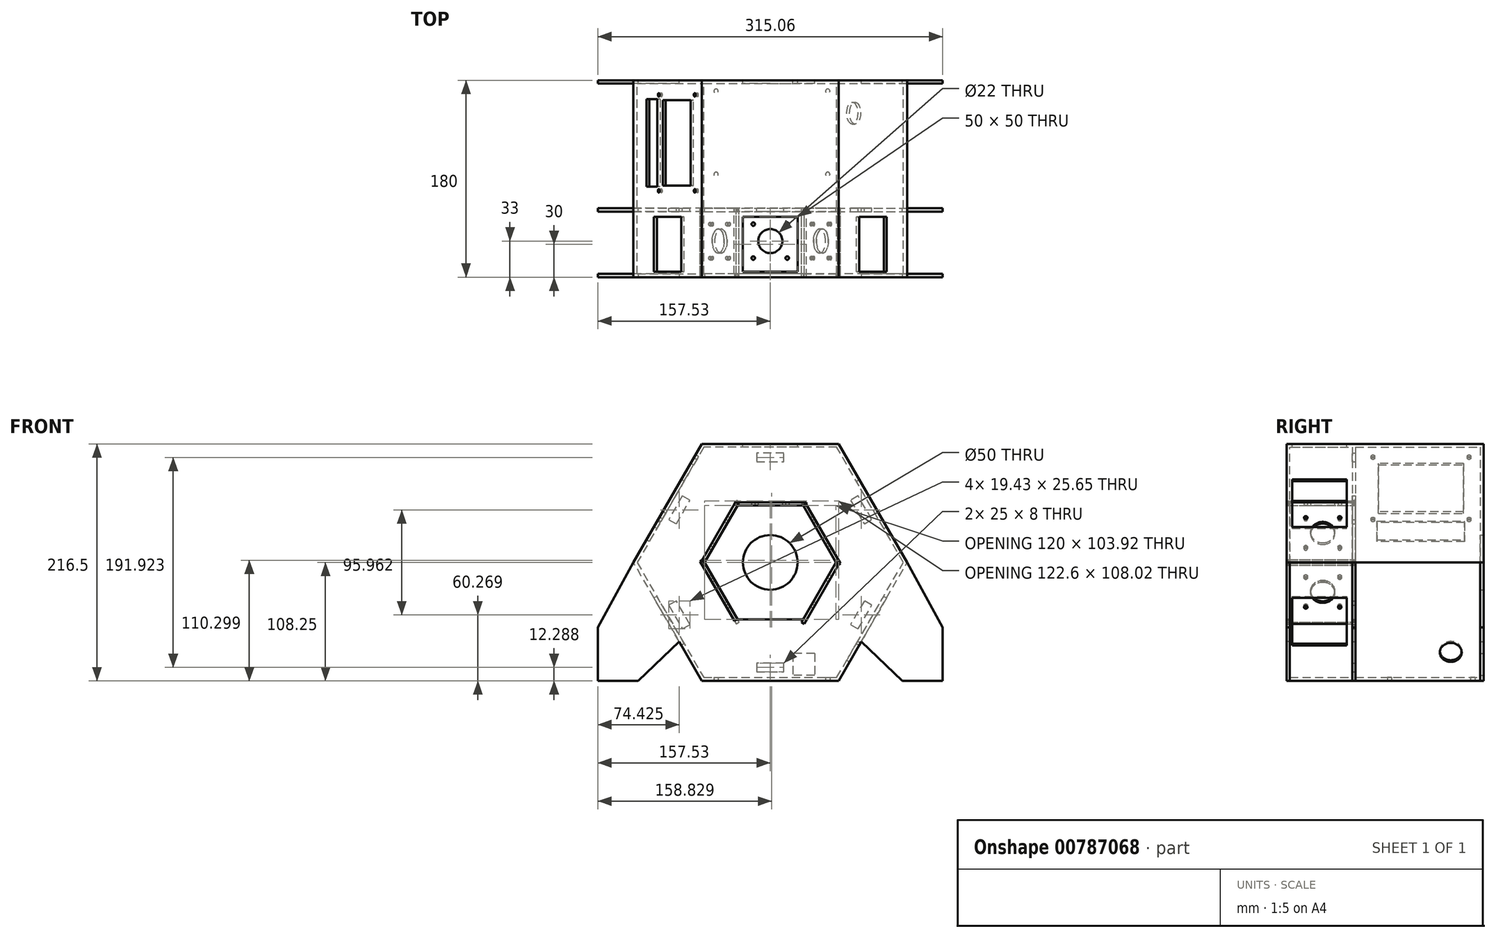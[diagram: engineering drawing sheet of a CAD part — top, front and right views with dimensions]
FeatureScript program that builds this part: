
annotation { "Feature Type Name" : "Feature", "Feature Type Description" : "" }
export const myFeature = defineFeature(function(context is Context, id is Id, definition is map)
    precondition{}
    {
        {
            var Q0;
            Q0=qCreatedBy(makeId("Front.planeOp"),FACE);
            var sketch = newSketch(context, id + "F0", { "sketchPlane" : qUnion([Q0])});
            skCircle(sketch, "E0.cCircle", {"center": v(0, 0) * mm, "radius": 108.25 * mm, "construction": true});
            skLineSegment(sketch, "E0.0", {"start": v(62.5, 108.25) * mm, "end": v(125, 0) * mm});
            skLineSegment(sketch, "E0.1", {"start": v(125, 0) * mm, "end": v(62.5, -108.25) * mm});
            skLineSegment(sketch, "E0.2", {"start": v(62.5, -108.25) * mm, "end": v(-62.5, -108.25) * mm});
            skLineSegment(sketch, "E0.3", {"start": v(-62.5, -108.25) * mm, "end": v(-125, 0) * mm});
            skLineSegment(sketch, "E0.4", {"start": v(-125, 0) * mm, "end": v(-62.5, 108.25) * mm});
            skLineSegment(sketch, "E0.5", {"start": v(-62.5, 108.25) * mm, "end": v(62.5, 108.25) * mm});
            skPoint(sketch, "E0.0.midPoint", {"position": v(93.75, 54.13) * mm});
            skSolve(sketch);
        }
        {
            var Q0;
            Q0=makeQuery(id+"F0.imprint","IMPRINT",FACE,{"disambiguationData":[TD([[makeQuery(id+"F0.imprint","IMPRINT",EDGE,{"derivedFrom":sQuery(id+"F0.wireOp",EDGE,"E0.0")}),-1.0]])]});
            extrude(context, id + "F1", {"entities" : qUnion([Q0]), "depth" : 180 * mm, "offsetDistance" : 25 * mm});
        }
        {
            var Q0;
            Q0=makeQuery(id+"F1.opExtrude","CAP_FACE",FACE,{"disambiguationData":[OSD([sQuery(id+"F0.wireOp",EDGE,"E0.0"),sQuery(id+"F0.wireOp",EDGE,"E0.1"),sQuery(id+"F0.wireOp",EDGE,"E0.2"),sQuery(id+"F0.wireOp",EDGE,"E0.3"),sQuery(id+"F0.wireOp",EDGE,"E0.4"),sQuery(id+"F0.wireOp",EDGE,"E0.5")])],"isStart":false});
            shell(context, id + "F2", {"entities" : qUnion([Q0]), "thickness" : 3 * mm});
        }
        {
            var Q0;
            Q0=makeQuery(id+"F1.opExtrude","CAP_FACE",FACE,{"disambiguationData":[OSD([sQuery(id+"F0.wireOp",EDGE,"E0.0"),sQuery(id+"F0.wireOp",EDGE,"E0.1"),sQuery(id+"F0.wireOp",EDGE,"E0.2"),sQuery(id+"F0.wireOp",EDGE,"E0.3"),sQuery(id+"F0.wireOp",EDGE,"E0.4"),sQuery(id+"F0.wireOp",EDGE,"E0.5")])],"isStart":false});
            var sketch = newSketch(context, id + "F3", { "sketchPlane" : qUnion([Q0])});
            skLineSegment(sketch, "E1.0", {"start": v(-60.77, 105.25) * mm, "end": v(60.77, 105.25) * mm});
            skLineSegment(sketch, "E2.0", {"start": v(60.77, 105.25) * mm, "end": v(121.54, 0) * mm});
            skLineSegment(sketch, "E3.0", {"start": v(121.54, 0) * mm, "end": v(60.77, -105.25) * mm});
            skLineSegment(sketch, "E3.1", {"start": v(60.77, -105.25) * mm, "end": v(-60.77, -105.25) * mm});
            skLineSegment(sketch, "E3.2", {"start": v(-60.77, -105.25) * mm, "end": v(-121.54, 0) * mm});
            skLineSegment(sketch, "E3.3", {"start": v(-121.54, 0) * mm, "end": v(-60.77, 105.25) * mm});
            skCircle(sketch, "E4.cCircle", {"center": v(0, 0) * mm, "radius": 51.96 * mm, "construction": true});
            skLineSegment(sketch, "E4.0", {"start": v(60, 0) * mm, "end": v(30, -51.96) * mm});
            skLineSegment(sketch, "E4.1", {"start": v(30, -51.96) * mm, "end": v(-30, -51.96) * mm});
            skLineSegment(sketch, "E4.2", {"start": v(-30, -51.96) * mm, "end": v(-60, 0) * mm});
            skLineSegment(sketch, "E4.3", {"start": v(-60, 0) * mm, "end": v(-30, 51.96) * mm});
            skLineSegment(sketch, "E4.4", {"start": v(-30, 51.96) * mm, "end": v(30, 51.96) * mm});
            skLineSegment(sketch, "E4.5", {"start": v(30, 51.96) * mm, "end": v(60, 0) * mm});
            skPoint(sketch, "E4.0.midPoint", {"position": v(45, -25.98) * mm});
            skSolve(sketch);
        }
        {
            var Q0;
            Q0=makeQuery(id+"F3.imprint","IMPRINT",FACE,{"disambiguationData":[TD([[makeQuery(id+"F3.imprint","IMPRINT",EDGE,{"derivedFrom":sQuery(id+"F3.wireOp",EDGE,"E1.0")}),-1.0]])]});
            extrude(context, id + "F4", {"entities" : qUnion([Q0]), "operationType" : NewBodyOperationType.ADD, "oppositeDirection" : true, "depth" : 3 * mm, "offsetDistance" : 25 * mm});
        }
        {
            var Q0;
            Q0=makeQuery(id+"F1.opExtrude","CAP_FACE",FACE,{"disambiguationData":[OSD([sQuery(id+"F0.wireOp",EDGE,"E0.0"),sQuery(id+"F0.wireOp",EDGE,"E0.1"),sQuery(id+"F0.wireOp",EDGE,"E0.2"),sQuery(id+"F0.wireOp",EDGE,"E0.3"),sQuery(id+"F0.wireOp",EDGE,"E0.4"),sQuery(id+"F0.wireOp",EDGE,"E0.5")])],"isStart":true});
            var sketch = newSketch(context, id + "F5", { "sketchPlane" : qUnion([Q0])});
            skPoint(sketch, "E5", {"position": v(0, 0) * mm});
            skSolve(sketch);
        }
        {
            var Q0;
            Q0=sQuery(id+"F5.wireOp",VERTEX,"E5");
            var Q1;
            Q1=makeQuery(id+"F1.opExtrude","SWEPT_BODY",BODY,{"disambiguationData":[OSD([sQuery(id+"F0.wireOp",EDGE,"E0.0"),sQuery(id+"F0.wireOp",EDGE,"E0.1"),sQuery(id+"F0.wireOp",EDGE,"E0.2"),sQuery(id+"F0.wireOp",EDGE,"E0.3"),sQuery(id+"F0.wireOp",EDGE,"E0.4"),sQuery(id+"F0.wireOp",EDGE,"E0.5")])]});
            hole(context, id + "F6", {"style" : HoleStyle.SIMPLE, "endStyle" : HoleEndStyle.THROUGH, "holeDiameter" : 50 * mm, "majorDiameter" : 5 * mm, "isTappedThrough" : true, "tappedDepth" : 12 * mm, "tapClearance" : 3, "locations" : qUnion([Q0]), "scope" : qUnion([Q1])});
        }
        {
            var Q0;
            Q0=makeQuery(id+"F4.opExtrude","SWEPT_FACE",FACE,{"disambiguationData":[OSD([sQuery(id+"F3.wireOp",EDGE,"E4.5")])]});
            var sketch = newSketch(context, id + "F7", { "sketchPlane" : qUnion([Q0])});
            skLineSegment(sketch, "E6.bottom", {"start": v(177, 30) * mm, "end": v(117, 30) * mm});
            skLineSegment(sketch, "E6.top", {"start": v(180, -30) * mm, "end": v(117, -30) * mm});
            skLineSegment(sketch, "E6.left", {"start": v(180, 30) * mm, "end": v(180, -30) * mm});
            skLineSegment(sketch, "E6.right", {"start": v(117, 30) * mm, "end": v(117, -30) * mm});
            skCircle(sketch, "E7", {"center": v(147, 0) * mm, "radius": 11 * mm});
            skCircle(sketch, "E8", {"center": v(162.5, 15.5) * mm, "radius": 1.6 * mm});
            skCircle(sketch, "E9", {"center": v(162.5, -15.5) * mm, "radius": 1.6 * mm});
            skCircle(sketch, "E10", {"center": v(131.5, -15.5) * mm, "radius": 1.6 * mm});
            skCircle(sketch, "E11", {"center": v(131.5, 15.5) * mm, "radius": 1.6 * mm});
            skLineSegment(sketch, "E12.top", {"start": v(177, 33) * mm, "end": v(117, 33) * mm});
            skLineSegment(sketch, "E12.left", {"start": v(177, 30) * mm, "end": v(177, 33) * mm});
            skLineSegment(sketch, "E12.right", {"start": v(117, 30) * mm, "end": v(117, 33) * mm});
            skLineSegment(sketch, "E13.bottom", {"start": v(180, -30) * mm, "end": v(120, -30) * mm});
            skLineSegment(sketch, "E13.top", {"start": v(180, -33) * mm, "end": v(120, -33) * mm});
            skLineSegment(sketch, "E13.left", {"start": v(180, -30) * mm, "end": v(180, -33) * mm});
            skLineSegment(sketch, "E13.right", {"start": v(120, -30) * mm, "end": v(120, -33) * mm});
            skSolve(sketch);
        }
        {
            var Q0;
            Q0=makeQuery(id+"F7.imprint","IMPRINT",FACE,{"disambiguationData":[TD([[makeQuery(id+"F7.imprint","IMPRINT",EDGE,{"derivedFrom":sQuery(id+"F7.wireOp",EDGE,"E6.bottom")}),-1.0]])]});
            var Q1;
            {var subQ0=sQuery(id+"F7.wireOp",EDGE,"E6.top");Q1=makeQuery(id+"F7.imprint","IMPRINT",FACE,{"disambiguationData":[TD([[makeQuery(id+"F7.imprint","IMPRINT",EDGE,{"derivedFrom":subQ0}),-1.0]])]});}
            var Q2;
            {var subQ0=sQuery(id+"F7.wireOp",EDGE,"E6.left");Q2=makeQuery(id+"F7.imprint","IMPRINT",FACE,{"disambiguationData":[TD([[makeQuery(id+"F7.imprint","IMPRINT",EDGE,{"derivedFrom":subQ0}),-1.0]])]});}
            var Q3;
            Q3=makeQuery(id+"F7.imprint","IMPRINT",FACE,{"disambiguationData":[TD([[makeQuery(id+"F7.imprint","IMPRINT",EDGE,{"derivedFrom":sQuery(id+"F7.wireOp",EDGE,"E13.top")}),-1.0]])]});
            extrude(context, id + "F8", {"entities" : qUnion([Q0, Q1, Q2, Q3]), "oppositeDirection" : true, "depth" : 3 * mm, "offsetDistance" : 25 * mm});
        }
        {
            var Q0;
            Q0=qCreatedBy(makeId("Right.planeOp"),FACE);
            var sketch = newSketch(context, id + "F9", { "sketchPlane" : qUnion([Q0])});
            skLineSegment(sketch, "E14", {"start": v(0, 0) * mm, "end": v(-423.8, 0) * mm, "construction": true});
            skSolve(sketch);
        }
        {
            var Q0;
            Q0=makeQuery(id+"F8.opExtrude","SWEPT_BODY",BODY,{"disambiguationData":[OSD([sQuery(id+"F7.wireOp",EDGE,"E6.bottom"),sQuery(id+"F7.wireOp",EDGE,"E6.top"),sQuery(id+"F7.wireOp",EDGE,"E6.left"),sQuery(id+"F7.wireOp",EDGE,"E6.right"),sQuery(id+"F7.wireOp",EDGE,"E7"),sQuery(id+"F7.wireOp",EDGE,"E8"),sQuery(id+"F7.wireOp",EDGE,"E9"),sQuery(id+"F7.wireOp",EDGE,"E10"),sQuery(id+"F7.wireOp",EDGE,"E11")])]});
            var Q1;
            Q1=sQuery(id+"F9.wireOp",EDGE,"E14");
            circularPattern(context, id + "F10", {"entities" : qUnion([Q0]), "axis" : qUnion([Q1]), "angle" : 360 * degree, "instanceCount" : 6, "equalSpace" : true});
        }
        {
            var Q0;
            Q0=makeQuery(id+"F10.opPattern","COPY",BODY,{"derivedFrom":makeQuery(id+"F8.opExtrude","SWEPT_BODY",BODY,{"disambiguationData":[OSD([sQuery(id+"F7.wireOp",EDGE,"E6.bottom"),sQuery(id+"F7.wireOp",EDGE,"E6.top"),sQuery(id+"F7.wireOp",EDGE,"E6.left"),sQuery(id+"F7.wireOp",EDGE,"E6.right"),sQuery(id+"F7.wireOp",EDGE,"E7"),sQuery(id+"F7.wireOp",EDGE,"E8"),sQuery(id+"F7.wireOp",EDGE,"E9"),sQuery(id+"F7.wireOp",EDGE,"E10"),sQuery(id+"F7.wireOp",EDGE,"E11")])]}),"instanceName":"4"});
            deleteBodies(context, id + "F11", {"entities" : qUnion([Q0])});
        }
        {
            var Q0;
            Q0=makeQuery(id+"F8.opExtrude","SWEPT_FACE",FACE,{"disambiguationData":[OSD([sQuery(id+"F7.wireOp",EDGE,"E6.right"),sQuery(id+"F7.wireOp",EDGE,"E12.right")])]});
            var sketch = newSketch(context, id + "F12", { "sketchPlane" : qUnion([Q0])});
            skLineSegment(sketch, "E15.0", {"start": v(-60, 0) * mm, "end": v(-28.5, 54.56) * mm});
            skLineSegment(sketch, "E16.0", {"start": v(-62.5, 108.25) * mm, "end": v(-125, 0) * mm});
            skLineSegment(sketch, "E17.0", {"start": v(62.5, 108.25) * mm, "end": v(-62.5, 108.25) * mm});
            skLineSegment(sketch, "E18.0", {"start": v(125, 0) * mm, "end": v(62.5, 108.25) * mm});
            skLineSegment(sketch, "E18.1", {"start": v(62.5, -108.25) * mm, "end": v(125, 0) * mm});
            skLineSegment(sketch, "E18.2", {"start": v(-62.5, -108.25) * mm, "end": v(62.5, -108.25) * mm});
            skLineSegment(sketch, "E18.3", {"start": v(-125, 0) * mm, "end": v(-62.5, -108.25) * mm});
            skLineSegment(sketch, "E19.0", {"start": v(-30, 51.96) * mm, "end": v(33, 51.96) * mm});
            skLineSegment(sketch, "E19.1", {"start": v(30, 51.96) * mm, "end": v(61.5, -2.6) * mm});
            skLineSegment(sketch, "E20.0", {"start": v(60, 0) * mm, "end": v(28.5, -54.56) * mm});
            skLineSegment(sketch, "E20.1", {"start": v(-30, -51.96) * mm, "end": v(30, -51.96) * mm});
            skLineSegment(sketch, "E20.2", {"start": v(-30, -51.96) * mm, "end": v(-61.5, 2.6) * mm});
            skSolve(sketch);
        }
        {
            var Q0;
            Q0=makeQuery(id+"F12.imprint","IMPRINT",FACE,{"disambiguationData":[TD([[makeQuery(id+"F12.imprint","IMPRINT",EDGE,{"derivedFrom":sQuery(id+"F12.wireOp",EDGE,"E16.0")}),1.0]])]});
            extrude(context, id + "F13", {"entities" : qUnion([Q0]), "oppositeDirection" : true, "depth" : 3 * mm, "offsetDistance" : 25 * mm});
        }
        {
            var Q0;
            Q0=makeQuery(id+"F1.opExtrude","SWEPT_FACE",FACE,{"disambiguationData":[OSD([sQuery(id+"F0.wireOp",EDGE,"E0.4")])]});
            var sketch = newSketch(context, id + "F14", { "sketchPlane" : qUnion([Q0])});
            skLineSegment(sketch, "E21.bottom", {"start": v(18.19, 42.08) * mm, "end": v(96.19, 42.08) * mm});
            skLineSegment(sketch, "E21.top", {"start": v(18.19, -8.92) * mm, "end": v(96.19, -8.92) * mm});
            skLineSegment(sketch, "E21.left", {"start": v(18.19, 42.08) * mm, "end": v(18.19, -8.92) * mm});
            skLineSegment(sketch, "E21.right", {"start": v(96.19, 42.08) * mm, "end": v(96.19, -8.92) * mm});
            skCircle(sketch, "E22", {"center": v(13.29, -16.32) * mm, "radius": 1.6 * mm});
            skCircle(sketch, "E23", {"center": v(13.29, 49.48) * mm, "radius": 1.6 * mm});
            skCircle(sketch, "E24", {"center": v(101.09, 49.48) * mm, "radius": 1.6 * mm});
            skCircle(sketch, "E25", {"center": v(101.09, -16.32) * mm, "radius": 1.6 * mm});
            skLineSegment(sketch, "E26.bottom", {"start": v(97.37, -38.8) * mm, "end": v(17.37, -38.8) * mm});
            skLineSegment(sketch, "E26.top", {"start": v(97.37, -18.8) * mm, "end": v(17.37, -18.8) * mm});
            skLineSegment(sketch, "E26.left", {"start": v(97.37, -38.8) * mm, "end": v(97.37, -18.8) * mm});
            skLineSegment(sketch, "E26.right", {"start": v(17.37, -38.8) * mm, "end": v(17.37, -18.8) * mm});
            skPoint(sketch, "E26.middle", {"position": v(57.37, -28.8) * mm});
            skSolve(sketch);
        }
        {
            var Q0;
            Q0 = qSketchRegion(id + "F14", true);
            extrude(context, id + "F15", {"entities" : qUnion([Q0]), "operationType" : NewBodyOperationType.REMOVE, "endBound" : BoundingType.UP_TO_NEXT, "oppositeDirection" : true, "depth" : 25 * mm, "offsetDistance" : 25 * mm});
        }
        {
            var Q0;
            Q0=makeQuery(id+"F1.opExtrude","SWEPT_FACE",FACE,{"disambiguationData":[OSD([sQuery(id+"F0.wireOp",EDGE,"E0.1")])]});
            var sketch = newSketch(context, id + "F16", { "sketchPlane" : qUnion([Q0])});
            skPoint(sketch, "E27", {"position": v(-30, -32.5) * mm});
            skSolve(sketch);
        }
        {
            var Q0;
            Q0=sQuery(id+"F16.wireOp",VERTEX,"E27");
            var Q1;
            Q1=makeQuery(id+"F1.opExtrude","SWEPT_BODY",BODY,{"disambiguationData":[OSD([sQuery(id+"F0.wireOp",EDGE,"E0.0"),sQuery(id+"F0.wireOp",EDGE,"E0.1"),sQuery(id+"F0.wireOp",EDGE,"E0.2"),sQuery(id+"F0.wireOp",EDGE,"E0.3"),sQuery(id+"F0.wireOp",EDGE,"E0.4"),sQuery(id+"F0.wireOp",EDGE,"E0.5")])]});
            hole(context, id + "F17", {"style" : HoleStyle.SIMPLE, "endStyle" : HoleEndStyle.BLIND, "holeDiameter" : 20 * mm, "majorDiameter" : 5 * mm, "holeDepth" : 3 * mm, "isTappedThrough" : true, "tappedDepth" : 12 * mm, "tapClearance" : 3, "locations" : qUnion([Q0]), "scope" : qUnion([Q1])});
        }
        {
            var Q0;
            Q0=makeQuery(id+"F1.opExtrude","CAP_FACE",FACE,{"disambiguationData":[OSD([sQuery(id+"F0.wireOp",EDGE,"E0.0"),sQuery(id+"F0.wireOp",EDGE,"E0.1"),sQuery(id+"F0.wireOp",EDGE,"E0.2"),sQuery(id+"F0.wireOp",EDGE,"E0.3"),sQuery(id+"F0.wireOp",EDGE,"E0.4"),sQuery(id+"F0.wireOp",EDGE,"E0.5")])],"isStart":true});
            var sketch = newSketch(context, id + "F18", { "sketchPlane" : qUnion([Q0])});
            skLineSegment(sketch, "E28.bottom", {"start": v(-40.5, -83.25) * mm, "end": v(-20.5, -83.25) * mm});
            skLineSegment(sketch, "E28.top", {"start": v(-40.5, -103.25) * mm, "end": v(-20.5, -103.25) * mm});
            skLineSegment(sketch, "E28.left", {"start": v(-40.5, -83.25) * mm, "end": v(-40.5, -103.25) * mm});
            skLineSegment(sketch, "E28.right", {"start": v(-20.5, -83.25) * mm, "end": v(-20.5, -103.25) * mm});
            skSolve(sketch);
        }
        {
            var Q0;
            Q0=makeQuery(id+"F18.imprint","IMPRINT",FACE,{"disambiguationData":[TD([[makeQuery(id+"F18.imprint","IMPRINT",EDGE,{"derivedFrom":sQuery(id+"F18.wireOp",EDGE,"E28.bottom")}),-1.0]])]});
            extrude(context, id + "F19", {"entities" : qUnion([Q0]), "operationType" : NewBodyOperationType.REMOVE, "endBound" : BoundingType.UP_TO_NEXT, "oppositeDirection" : true, "depth" : 25 * mm, "offsetDistance" : 25 * mm});
        }
        {
            var Q0;
            Q0=makeQuery(id+"F13.opExtrude","CAP_FACE",FACE,{"disambiguationData":[OSD([sQuery(id+"F7.wireOp",EDGE,"E6.top"),sQuery(id+"F7.wireOp",EDGE,"E6.right"),sQuery(id+"F7.wireOp",EDGE,"E12.top"),sQuery(id+"F7.wireOp",EDGE,"E12.right"),sQuery(id+"F12.wireOp",EDGE,"E15.0"),sQuery(id+"F12.wireOp",EDGE,"E16.0"),sQuery(id+"F12.wireOp",EDGE,"E17.0"),sQuery(id+"F12.wireOp",EDGE,"E18.0"),sQuery(id+"F12.wireOp",EDGE,"E18.1"),sQuery(id+"F12.wireOp",EDGE,"E18.2"),sQuery(id+"F12.wireOp",EDGE,"E18.3"),sQuery(id+"F12.wireOp",EDGE,"E19.0"),sQuery(id+"F12.wireOp",EDGE,"E19.1"),sQuery(id+"F12.wireOp",EDGE,"E20.0"),sQuery(id+"F12.wireOp",EDGE,"E20.1"),sQuery(id+"F12.wireOp",EDGE,"E20.2")])],"isStart":true});
            var sketch = newSketch(context, id + "F20", { "sketchPlane" : qUnion([Q0])});
            skLineSegment(sketch, "E29.bottom", {"start": v(12.5, 99.96) * mm, "end": v(-12.5, 99.96) * mm});
            skLineSegment(sketch, "E29.top", {"start": v(12.5, 91.96) * mm, "end": v(-12.5, 91.96) * mm});
            skLineSegment(sketch, "E29.left", {"start": v(12.5, 99.96) * mm, "end": v(12.5, 91.96) * mm});
            skLineSegment(sketch, "E29.right", {"start": v(-12.5, 99.96) * mm, "end": v(-12.5, 91.96) * mm});
            skPoint(sketch, "E29.middle", {"position": v(0, 95.96) * mm});
            skLineSegment(sketch, "E30.1.0", {"start": v(-80.32, 60.8) * mm, "end": v(-73.4, 56.8) * mm});
            skLineSegment(sketch, "E30.1.1", {"start": v(-80.32, 60.8) * mm, "end": v(-92.82, 39.16) * mm});
            skLineSegment(sketch, "E30.1.2", {"start": v(-92.82, 39.16) * mm, "end": v(-85.9, 35.16) * mm});
            skLineSegment(sketch, "E30.1.3", {"start": v(-73.4, 56.8) * mm, "end": v(-85.9, 35.16) * mm});
            skLineSegment(sketch, "E30.2.0", {"start": v(-92.82, -39.16) * mm, "end": v(-85.9, -35.16) * mm});
            skLineSegment(sketch, "E30.2.1", {"start": v(-92.82, -39.16) * mm, "end": v(-80.32, -60.8) * mm});
            skLineSegment(sketch, "E30.2.2", {"start": v(-80.32, -60.8) * mm, "end": v(-73.4, -56.8) * mm});
            skLineSegment(sketch, "E30.2.3", {"start": v(-85.9, -35.16) * mm, "end": v(-73.4, -56.8) * mm});
            skLineSegment(sketch, "E30.3.0", {"start": v(-12.5, -99.96) * mm, "end": v(-12.5, -91.96) * mm});
            skLineSegment(sketch, "E30.3.1", {"start": v(-12.5, -99.96) * mm, "end": v(12.5, -99.96) * mm});
            skLineSegment(sketch, "E30.3.2", {"start": v(12.5, -99.96) * mm, "end": v(12.5, -91.96) * mm});
            skLineSegment(sketch, "E30.3.3", {"start": v(-12.5, -91.96) * mm, "end": v(12.5, -91.96) * mm});
            skLineSegment(sketch, "E30.4.0", {"start": v(80.32, -60.8) * mm, "end": v(73.4, -56.8) * mm});
            skLineSegment(sketch, "E30.4.1", {"start": v(80.32, -60.8) * mm, "end": v(92.82, -39.16) * mm});
            skLineSegment(sketch, "E30.4.2", {"start": v(92.82, -39.16) * mm, "end": v(85.9, -35.16) * mm});
            skLineSegment(sketch, "E30.4.3", {"start": v(73.4, -56.8) * mm, "end": v(85.9, -35.16) * mm});
            skLineSegment(sketch, "E30.5.0", {"start": v(92.82, 39.16) * mm, "end": v(85.9, 35.16) * mm});
            skLineSegment(sketch, "E30.5.1", {"start": v(92.82, 39.16) * mm, "end": v(80.32, 60.8) * mm});
            skLineSegment(sketch, "E30.5.2", {"start": v(80.32, 60.8) * mm, "end": v(73.4, 56.8) * mm});
            skLineSegment(sketch, "E30.5.3", {"start": v(85.9, 35.16) * mm, "end": v(73.4, 56.8) * mm});
            skPoint(sketch, "E30.center", {"position": v(0, 0) * mm});
            skSolve(sketch);
        }
        {
            var Q0;
            Q0 = qSketchRegion(id + "F20", true);
            extrude(context, id + "F21", {"entities" : qUnion([Q0]), "operationType" : NewBodyOperationType.REMOVE, "endBound" : BoundingType.UP_TO_NEXT, "oppositeDirection" : true, "depth" : 25 * mm, "offsetDistance" : 25 * mm});
        }
        {
            var Q0;
            Q0=makeQuery(id+"F1.opExtrude","SWEPT_FACE",FACE,{"disambiguationData":[OSD([sQuery(id+"F0.wireOp",EDGE,"E0.2")])]});
            var sketch = newSketch(context, id + "F22", { "sketchPlane" : qUnion([Q0])});
            skLineSegment(sketch, "E31.bottom", {"start": v(-49.5, 10) * mm, "end": v(52.5, 10) * mm});
            skLineSegment(sketch, "E31.top", {"start": v(-49.5, 86) * mm, "end": v(52.5, 86) * mm});
            skLineSegment(sketch, "E31.left", {"start": v(-49.5, 10) * mm, "end": v(-49.5, 86) * mm});
            skLineSegment(sketch, "E31.right", {"start": v(52.5, 10) * mm, "end": v(52.5, 86) * mm});
            skCircle(sketch, "E32", {"center": v(-49.5, 10) * mm, "radius": 2 * mm});
            skCircle(sketch, "E33", {"center": v(-49.5, 86) * mm, "radius": 2 * mm});
            skCircle(sketch, "E34", {"center": v(52.5, 86) * mm, "radius": 2 * mm});
            skCircle(sketch, "E35", {"center": v(52.5, 10) * mm, "radius": 2 * mm});
            skSolve(sketch);
        }
        {
            var Q0;
            {var subQ0=sQuery(id+"F22.wireOp",EDGE,"E31.right");var subQ1=sQuery(id+"F22.wireOp",EDGE,"E31.bottom");var subQ2=makeQuery(id+"F22.imprint","INTERSECT",VERTEX,{"derivedFrom":[subQ1,subQ0]});Q0=makeQuery(id+"F22.imprint","IMPRINT",FACE,{"disambiguationData":[TD([[makeQuery(id+"F22.imprint","IMPRINT",EDGE,{"disambiguationData":[TD([[subQ2,1.0]])],"derivedFrom":subQ1}),-1.0]])]});}
            var Q1;
            {var subQ0=sQuery(id+"F22.wireOp",EDGE,"E31.right");var subQ1=sQuery(id+"F22.wireOp",EDGE,"E31.bottom");var subQ2=makeQuery(id+"F22.imprint","INTERSECT",VERTEX,{"derivedFrom":[subQ1,subQ0]});Q1=makeQuery(id+"F22.imprint","IMPRINT",FACE,{"disambiguationData":[TD([[makeQuery(id+"F22.imprint","IMPRINT",EDGE,{"disambiguationData":[TD([[subQ2,1.0]])],"derivedFrom":subQ1}),1.0]])]});}
            var Q2;
            {var subQ0=sQuery(id+"F22.wireOp",EDGE,"E31.left");var subQ1=sQuery(id+"F22.wireOp",EDGE,"E31.bottom");var subQ2=makeQuery(id+"F22.imprint","INTERSECT",VERTEX,{"derivedFrom":[subQ1,subQ0]});Q2=makeQuery(id+"F22.imprint","IMPRINT",FACE,{"disambiguationData":[TD([[makeQuery(id+"F22.imprint","IMPRINT",EDGE,{"disambiguationData":[TD([[subQ2,-1.0]])],"derivedFrom":subQ1}),1.0]])]});}
            var Q3;
            {var subQ0=sQuery(id+"F22.wireOp",EDGE,"E31.left");var subQ1=sQuery(id+"F22.wireOp",EDGE,"E31.bottom");var subQ2=makeQuery(id+"F22.imprint","INTERSECT",VERTEX,{"derivedFrom":[subQ1,subQ0]});Q3=makeQuery(id+"F22.imprint","IMPRINT",FACE,{"disambiguationData":[TD([[makeQuery(id+"F22.imprint","IMPRINT",EDGE,{"disambiguationData":[TD([[subQ2,-1.0]])],"derivedFrom":subQ1}),-1.0]])]});}
            var Q4;
            {var subQ0=sQuery(id+"F22.wireOp",EDGE,"E31.left");var subQ1=sQuery(id+"F22.wireOp",EDGE,"E31.top");var subQ2=makeQuery(id+"F22.imprint","INTERSECT",VERTEX,{"derivedFrom":[subQ1,subQ0]});Q4=makeQuery(id+"F22.imprint","IMPRINT",FACE,{"disambiguationData":[TD([[makeQuery(id+"F22.imprint","IMPRINT",EDGE,{"disambiguationData":[TD([[subQ2,-1.0]])],"derivedFrom":subQ1}),1.0]])]});}
            var Q5;
            {var subQ0=sQuery(id+"F22.wireOp",EDGE,"E31.left");var subQ1=sQuery(id+"F22.wireOp",EDGE,"E31.top");var subQ2=makeQuery(id+"F22.imprint","INTERSECT",VERTEX,{"derivedFrom":[subQ1,subQ0]});Q5=makeQuery(id+"F22.imprint","IMPRINT",FACE,{"disambiguationData":[TD([[makeQuery(id+"F22.imprint","IMPRINT",EDGE,{"disambiguationData":[TD([[subQ2,-1.0]])],"derivedFrom":subQ1}),-1.0]])]});}
            var Q6;
            {var subQ0=sQuery(id+"F22.wireOp",EDGE,"E31.right");var subQ1=sQuery(id+"F22.wireOp",EDGE,"E31.top");var subQ2=makeQuery(id+"F22.imprint","INTERSECT",VERTEX,{"derivedFrom":[subQ1,subQ0]});Q6=makeQuery(id+"F22.imprint","IMPRINT",FACE,{"disambiguationData":[TD([[makeQuery(id+"F22.imprint","IMPRINT",EDGE,{"disambiguationData":[TD([[subQ2,1.0]])],"derivedFrom":subQ1}),1.0]])]});}
            var Q7;
            {var subQ0=sQuery(id+"F22.wireOp",EDGE,"E31.right");var subQ1=sQuery(id+"F22.wireOp",EDGE,"E31.top");var subQ2=makeQuery(id+"F22.imprint","INTERSECT",VERTEX,{"derivedFrom":[subQ1,subQ0]});Q7=makeQuery(id+"F22.imprint","IMPRINT",FACE,{"disambiguationData":[TD([[makeQuery(id+"F22.imprint","IMPRINT",EDGE,{"disambiguationData":[TD([[subQ2,1.0]])],"derivedFrom":subQ1}),-1.0]])]});}
            extrude(context, id + "F23", {"entities" : qUnion([Q0, Q1, Q2, Q3, Q4, Q5, Q6, Q7]), "operationType" : NewBodyOperationType.REMOVE, "endBound" : BoundingType.UP_TO_NEXT, "oppositeDirection" : true, "depth" : 25 * mm, "offsetDistance" : 25 * mm});
        }
        {
            var Q0;
            Q0=makeQuery(id+"F1.opExtrude","SWEPT_FACE",FACE,{"disambiguationData":[OSD([sQuery(id+"F0.wireOp",EDGE,"E0.3")])]});
            var sketch = newSketch(context, id + "F24", { "sketchPlane" : qUnion([Q0])});
            skLineSegment(sketch, "E36.bottom", {"start": v(125, 25) * mm, "end": v(175, 25) * mm});
            skLineSegment(sketch, "E36.top", {"start": v(125, -25) * mm, "end": v(175, -25) * mm});
            skLineSegment(sketch, "E36.left", {"start": v(125, 25) * mm, "end": v(125, -25) * mm});
            skLineSegment(sketch, "E36.right", {"start": v(175, 25) * mm, "end": v(175, -25) * mm});
            skSolve(sketch);
        }
        {
            var Q0;
            Q0 = qSketchRegion(id + "F24", true);
            extrude(context, id + "F25", {"entities" : qUnion([Q0]), "operationType" : NewBodyOperationType.REMOVE, "endBound" : BoundingType.UP_TO_NEXT, "oppositeDirection" : true, "depth" : 25 * mm, "offsetDistance" : 25 * mm});
        }
        {
            var Q0;
            Q0=makeQuery(id+"F1.opExtrude","SWEPT_FACE",FACE,{"disambiguationData":[OSD([sQuery(id+"F0.wireOp",EDGE,"E0.4")])]});
            var sketch = newSketch(context, id + "F26", { "sketchPlane" : qUnion([Q0])});
            skLineSegment(sketch, "E37.bottom", {"start": v(125, 25) * mm, "end": v(175, 25) * mm});
            skLineSegment(sketch, "E37.top", {"start": v(125, -25) * mm, "end": v(175, -25) * mm});
            skLineSegment(sketch, "E37.left", {"start": v(125, 25) * mm, "end": v(125, -25) * mm});
            skLineSegment(sketch, "E37.right", {"start": v(175, 25) * mm, "end": v(175, -25) * mm});
            skSolve(sketch);
        }
        {
            var Q0;
            Q0=makeQuery(id+"F26.imprint","IMPRINT",FACE,{"disambiguationData":[TD([[makeQuery(id+"F26.imprint","IMPRINT",EDGE,{"derivedFrom":sQuery(id+"F26.wireOp",EDGE,"E37.bottom")}),-1.0]])]});
            extrude(context, id + "F27", {"entities" : qUnion([Q0]), "operationType" : NewBodyOperationType.REMOVE, "endBound" : BoundingType.UP_TO_NEXT, "oppositeDirection" : true, "depth" : 25 * mm, "offsetDistance" : 25 * mm});
        }
        {
            var Q0;
            Q0=makeQuery(id+"F1.opExtrude","SWEPT_FACE",FACE,{"disambiguationData":[OSD([sQuery(id+"F0.wireOp",EDGE,"E0.5")])]});
            var sketch = newSketch(context, id + "F28", { "sketchPlane" : qUnion([Q0])});
            skLineSegment(sketch, "E38.bottom", {"start": v(-25, -125) * mm, "end": v(25, -125) * mm});
            skLineSegment(sketch, "E38.top", {"start": v(-25, -175) * mm, "end": v(25, -175) * mm});
            skLineSegment(sketch, "E38.left", {"start": v(-25, -125) * mm, "end": v(-25, -175) * mm});
            skLineSegment(sketch, "E38.right", {"start": v(25, -125) * mm, "end": v(25, -175) * mm});
            skSolve(sketch);
        }
        {
            var Q0;
            Q0=makeQuery(id+"F28.imprint","IMPRINT",FACE,{"disambiguationData":[TD([[makeQuery(id+"F28.imprint","IMPRINT",EDGE,{"derivedFrom":sQuery(id+"F28.wireOp",EDGE,"E38.bottom")}),-1.0]])]});
            extrude(context, id + "F29", {"entities" : qUnion([Q0]), "operationType" : NewBodyOperationType.REMOVE, "endBound" : BoundingType.UP_TO_NEXT, "oppositeDirection" : true, "depth" : 25 * mm, "offsetDistance" : 25 * mm});
        }
        {
            var Q0;
            Q0=makeQuery(id+"F1.opExtrude","SWEPT_FACE",FACE,{"disambiguationData":[OSD([sQuery(id+"F0.wireOp",EDGE,"E0.0")])]});
            var sketch = newSketch(context, id + "F30", { "sketchPlane" : qUnion([Q0])});
            skLineSegment(sketch, "E39.bottom", {"start": v(-125, 25) * mm, "end": v(-175, 25) * mm});
            skLineSegment(sketch, "E39.top", {"start": v(-125, -25) * mm, "end": v(-175, -25) * mm});
            skLineSegment(sketch, "E39.left", {"start": v(-125, 25) * mm, "end": v(-125, -25) * mm});
            skLineSegment(sketch, "E39.right", {"start": v(-175, 25) * mm, "end": v(-175, -25) * mm});
            skSolve(sketch);
        }
        {
            var Q0;
            Q0=makeQuery(id+"F30.imprint","IMPRINT",FACE,{"disambiguationData":[TD([[makeQuery(id+"F30.imprint","IMPRINT",EDGE,{"derivedFrom":sQuery(id+"F30.wireOp",EDGE,"E39.bottom")}),1.0]])]});
            extrude(context, id + "F31", {"entities" : qUnion([Q0]), "operationType" : NewBodyOperationType.REMOVE, "endBound" : BoundingType.UP_TO_NEXT, "oppositeDirection" : true, "depth" : 25 * mm, "offsetDistance" : 25 * mm});
        }
        {
            var Q0;
            Q0=makeQuery(id+"F1.opExtrude","SWEPT_FACE",FACE,{"disambiguationData":[OSD([sQuery(id+"F0.wireOp",EDGE,"E0.1")])]});
            var sketch = newSketch(context, id + "F32", { "sketchPlane" : qUnion([Q0])});
            skLineSegment(sketch, "E40.bottom", {"start": v(-125, 25) * mm, "end": v(-175, 25) * mm});
            skLineSegment(sketch, "E40.top", {"start": v(-125, -25) * mm, "end": v(-175, -25) * mm});
            skLineSegment(sketch, "E40.left", {"start": v(-125, 25) * mm, "end": v(-125, -25) * mm});
            skLineSegment(sketch, "E40.right", {"start": v(-175, 25) * mm, "end": v(-175, -25) * mm});
            skSolve(sketch);
        }
        {
            var Q0;
            Q0=makeQuery(id+"F32.imprint","IMPRINT",FACE,{"disambiguationData":[TD([[makeQuery(id+"F32.imprint","IMPRINT",EDGE,{"derivedFrom":sQuery(id+"F32.wireOp",EDGE,"E40.bottom")}),1.0]])]});
            extrude(context, id + "F33", {"entities" : qUnion([Q0]), "operationType" : NewBodyOperationType.REMOVE, "endBound" : BoundingType.UP_TO_NEXT, "oppositeDirection" : true, "depth" : 25 * mm, "offsetDistance" : 25 * mm});
        }
        {
            var Q0;
            Q0=makeQuery(id+"F4.boolean.opBoolean","MERGE",FACE,{"derivedFrom":[makeQuery(id+"F1.opExtrude","CAP_FACE",FACE,{"disambiguationData":[OSD([sQuery(id+"F0.wireOp",EDGE,"E0.0"),sQuery(id+"F0.wireOp",EDGE,"E0.1"),sQuery(id+"F0.wireOp",EDGE,"E0.2"),sQuery(id+"F0.wireOp",EDGE,"E0.3"),sQuery(id+"F0.wireOp",EDGE,"E0.4"),sQuery(id+"F0.wireOp",EDGE,"E0.5")])],"isStart":false}),makeQuery(id+"F4.opExtrude","CAP_FACE",FACE,{"disambiguationData":[OSD([sQuery(id+"F3.wireOp",EDGE,"E1.0"),sQuery(id+"F3.wireOp",EDGE,"E2.0"),sQuery(id+"F3.wireOp",EDGE,"E3.0"),sQuery(id+"F3.wireOp",EDGE,"E3.1"),sQuery(id+"F3.wireOp",EDGE,"E3.2"),sQuery(id+"F3.wireOp",EDGE,"E3.3"),sQuery(id+"F3.wireOp",EDGE,"E4.0"),sQuery(id+"F3.wireOp",EDGE,"E4.1"),sQuery(id+"F3.wireOp",EDGE,"E4.2"),sQuery(id+"F3.wireOp",EDGE,"E4.3"),sQuery(id+"F3.wireOp",EDGE,"E4.4"),sQuery(id+"F3.wireOp",EDGE,"E4.5")])],"isStart":true})]});
            var sketch = newSketch(context, id + "F34", { "sketchPlane" : qUnion([Q0])});
            skLineSegment(sketch, "E41", {"start": v(83.18, -72.44) * mm, "end": v(120.63, -108.25) * mm});
            skLineSegment(sketch, "E42", {"start": v(120.63, -108.25) * mm, "end": v(157.53, -108.25) * mm});
            skLineSegment(sketch, "E43", {"start": v(157.53, -108.25) * mm, "end": v(157.53, -59.53) * mm});
            skLineSegment(sketch, "E44", {"start": v(157.53, -59.53) * mm, "end": v(125, 0) * mm});
            skLineSegment(sketch, "E45", {"start": v(0, 108.25) * mm, "end": v(0, -108.25) * mm, "construction": true});
            skLineSegment(sketch, "E46.MirrorCS", {"start": v(-157.53, -59.53) * mm, "end": v(-125, 0) * mm});
            skLineSegment(sketch, "E47.MirrorCS", {"start": v(-157.53, -108.25) * mm, "end": v(-157.53, -59.53) * mm});
            skLineSegment(sketch, "E48.MirrorCS", {"start": v(-120.63, -108.25) * mm, "end": v(-157.53, -108.25) * mm});
            skLineSegment(sketch, "E49.MirrorCS", {"start": v(-83.18, -72.44) * mm, "end": v(-120.63, -108.25) * mm});
            skSolve(sketch);
        }
        {
            var Q0;
            {var subQ1=sQuery(id+"F34.wireOp",EDGE,"E46.MirrorCS");Q0=makeQuery(id+"F34.imprint","IMPRINT",FACE,{"disambiguationData":[TD([[makeQuery(id+"F34.imprint","IMPRINT",EDGE,{"derivedFrom":subQ1}),-1.0]])]});}
            var Q1;
            {var subQ1=sQuery(id+"F34.wireOp",EDGE,"E41");Q1=makeQuery(id+"F34.imprint","IMPRINT",FACE,{"disambiguationData":[TD([[makeQuery(id+"F34.imprint","IMPRINT",EDGE,{"derivedFrom":subQ1}),1.0]])]});}
            extrude(context, id + "F35", {"entities" : qUnion([Q0, Q1]), "operationType" : NewBodyOperationType.ADD, "oppositeDirection" : true, "depth" : 3 * mm, "offsetDistance" : 25 * mm});
        }
        {
            var Q0;
            Q0=makeQuery(id+"F1.opExtrude","CAP_FACE",FACE,{"disambiguationData":[OSD([sQuery(id+"F0.wireOp",EDGE,"E0.0"),sQuery(id+"F0.wireOp",EDGE,"E0.1"),sQuery(id+"F0.wireOp",EDGE,"E0.2"),sQuery(id+"F0.wireOp",EDGE,"E0.3"),sQuery(id+"F0.wireOp",EDGE,"E0.4"),sQuery(id+"F0.wireOp",EDGE,"E0.5")])],"isStart":true});
            var sketch = newSketch(context, id + "F36", { "sketchPlane" : qUnion([Q0])});
            skLineSegment(sketch, "E50.0", {"start": v(157.53, -59.53) * mm, "end": v(125, 0) * mm});
            skLineSegment(sketch, "E50.1", {"start": v(157.53, -108.25) * mm, "end": v(157.53, -59.53) * mm});
            skLineSegment(sketch, "E50.2", {"start": v(120.63, -108.25) * mm, "end": v(157.53, -108.25) * mm});
            skLineSegment(sketch, "E50.3", {"start": v(83.18, -72.44) * mm, "end": v(120.63, -108.25) * mm});
            skLineSegment(sketch, "E51.0", {"start": v(-157.53, -59.53) * mm, "end": v(-125, 0) * mm});
            skLineSegment(sketch, "E51.1", {"start": v(-157.53, -108.25) * mm, "end": v(-157.53, -59.53) * mm});
            skLineSegment(sketch, "E51.2", {"start": v(-120.63, -108.25) * mm, "end": v(-157.53, -108.25) * mm});
            skLineSegment(sketch, "E51.3", {"start": v(-83.18, -72.44) * mm, "end": v(-120.63, -108.25) * mm});
            skLineSegment(sketch, "E52", {"start": v(-125, 0) * mm, "end": v(-83.18, -72.44) * mm});
            skLineSegment(sketch, "E53", {"start": v(125, 0) * mm, "end": v(83.18, -72.44) * mm});
            skSolve(sketch);
        }
        {
            var Q0;
            Q0=makeQuery(id+"F36.imprint","IMPRINT",FACE,{"disambiguationData":[TD([[makeQuery(id+"F36.imprint","IMPRINT",EDGE,{"derivedFrom":sQuery(id+"F36.wireOp",EDGE,"E51.0")}),-1.0]])]});
            var Q1;
            Q1=makeQuery(id+"F36.imprint","IMPRINT",FACE,{"disambiguationData":[TD([[makeQuery(id+"F36.imprint","IMPRINT",EDGE,{"derivedFrom":sQuery(id+"F36.wireOp",EDGE,"E50.0")}),1.0]])]});
            extrude(context, id + "F37", {"entities" : qUnion([Q0, Q1]), "operationType" : NewBodyOperationType.ADD, "oppositeDirection" : true, "depth" : 3 * mm, "offsetDistance" : 25 * mm});
        }
        {
            var Q0;
            Q0=makeQuery(id+"F13.opExtrude","CAP_FACE",FACE,{"disambiguationData":[OSD([sQuery(id+"F7.wireOp",EDGE,"E6.top"),sQuery(id+"F7.wireOp",EDGE,"E6.right"),sQuery(id+"F7.wireOp",EDGE,"E12.top"),sQuery(id+"F7.wireOp",EDGE,"E12.right"),sQuery(id+"F12.wireOp",EDGE,"E15.0"),sQuery(id+"F12.wireOp",EDGE,"E16.0"),sQuery(id+"F12.wireOp",EDGE,"E17.0"),sQuery(id+"F12.wireOp",EDGE,"E18.0"),sQuery(id+"F12.wireOp",EDGE,"E18.1"),sQuery(id+"F12.wireOp",EDGE,"E18.2"),sQuery(id+"F12.wireOp",EDGE,"E18.3"),sQuery(id+"F12.wireOp",EDGE,"E19.0"),sQuery(id+"F12.wireOp",EDGE,"E19.1"),sQuery(id+"F12.wireOp",EDGE,"E20.0"),sQuery(id+"F12.wireOp",EDGE,"E20.1"),sQuery(id+"F12.wireOp",EDGE,"E20.2")])],"isStart":true});
            var sketch = newSketch(context, id + "F38", { "sketchPlane" : qUnion([Q0])});
            skLineSegment(sketch, "E54.0", {"start": v(-157.53, -59.53) * mm, "end": v(-125, 0) * mm});
            skLineSegment(sketch, "E54.1", {"start": v(-157.53, -108.25) * mm, "end": v(-157.53, -59.53) * mm});
            skLineSegment(sketch, "E54.2", {"start": v(-120.63, -108.25) * mm, "end": v(-157.53, -108.25) * mm});
            skLineSegment(sketch, "E54.3", {"start": v(-83.18, -72.44) * mm, "end": v(-120.63, -108.25) * mm});
            skLineSegment(sketch, "E54.4", {"start": v(-125, 0) * mm, "end": v(-83.18, -72.44) * mm});
            skLineSegment(sketch, "E55.0", {"start": v(157.53, -59.53) * mm, "end": v(125, 0) * mm});
            skLineSegment(sketch, "E55.1", {"start": v(157.53, -108.25) * mm, "end": v(157.53, -59.53) * mm});
            skLineSegment(sketch, "E55.2", {"start": v(120.63, -108.25) * mm, "end": v(157.53, -108.25) * mm});
            skLineSegment(sketch, "E55.3", {"start": v(83.18, -72.44) * mm, "end": v(120.63, -108.25) * mm});
            skLineSegment(sketch, "E55.4", {"start": v(83.18, -72.44) * mm, "end": v(125, 0) * mm});
            skSolve(sketch);
        }
        {
            var Q0;
            Q0=makeQuery(id+"F38.imprint","IMPRINT",FACE,{"disambiguationData":[TD([[makeQuery(id+"F38.imprint","IMPRINT",EDGE,{"derivedFrom":sQuery(id+"F38.wireOp",EDGE,"E55.0")}),1.0]])]});
            var Q1;
            Q1=makeQuery(id+"F38.imprint","IMPRINT",FACE,{"disambiguationData":[TD([[makeQuery(id+"F38.imprint","IMPRINT",EDGE,{"derivedFrom":sQuery(id+"F38.wireOp",EDGE,"E54.0")}),-1.0]])]});
            extrude(context, id + "F39", {"entities" : qUnion([Q0, Q1]), "operationType" : NewBodyOperationType.ADD, "oppositeDirection" : true, "depth" : 3 * mm, "offsetDistance" : 25 * mm});
        }
    });
